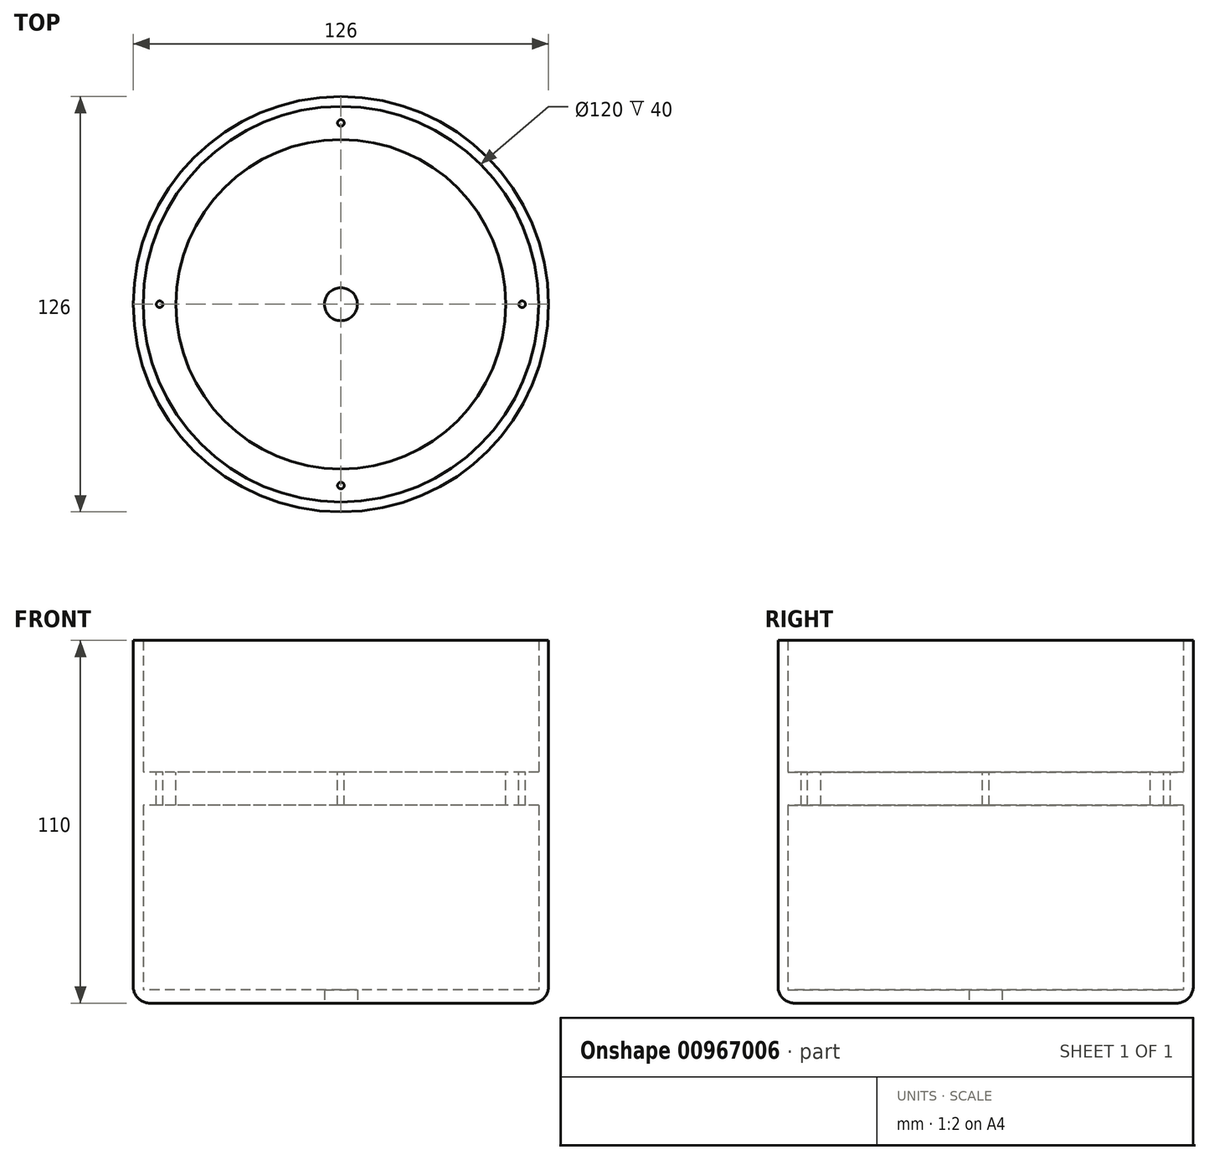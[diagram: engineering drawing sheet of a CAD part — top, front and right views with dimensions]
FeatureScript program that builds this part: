
annotation { "Feature Type Name" : "Feature", "Feature Type Description" : "" }
export const myFeature = defineFeature(function(context is Context, id is Id, definition is map)
    precondition{}
    {
        {
            var Q0;
            Q0=qCreatedBy(makeId("Top.planeOp"),FACE);
            var sketch = newSketch(context, id + "F0", { "sketchPlane" : qUnion([Q0])});
            skCircle(sketch, "E0", {"center": v(0, 0) * mm, "radius": 60 * mm});
            skCircle(sketch, "E1", {"center": v(0, 0) * mm, "radius": 63 * mm});
            skCircle(sketch, "E2", {"center": v(0, 0) * mm, "radius": 50 * mm});
            skCircle(sketch, "E3", {"center": v(0, 55) * mm, "radius": 1 * mm});
            skCircle(sketch, "E4", {"center": v(0, -55) * mm, "radius": 1 * mm});
            skCircle(sketch, "E5", {"center": v(55, 0) * mm, "radius": 1 * mm});
            skCircle(sketch, "E6", {"center": v(-55, 0) * mm, "radius": 1 * mm});
            skSolve(sketch);
        }
        {
            var Q0;
            Q0=makeQuery(id+"F0.imprint","IMPRINT",FACE,{"disambiguationData":[TD([[makeQuery(id+"F0.imprint","IMPRINT",EDGE,{"derivedFrom":sQuery(id+"F0.wireOp",EDGE,"E0")}),-1.0]])]});
            extrude(context, id + "F1", {"entities" : qUnion([Q0]), "depth" : 40 * mm, "offsetDistance" : 25 * mm});
        }
        {
            var Q0;
            Q0=makeQuery(id+"F0.imprint","IMPRINT",FACE,{"disambiguationData":[TD([[makeQuery(id+"F0.imprint","IMPRINT",EDGE,{"derivedFrom":sQuery(id+"F0.wireOp",EDGE,"E0")}),-1.0]])]});
            extrude(context, id + "F2", {"entities" : qUnion([Q0]), "operationType" : NewBodyOperationType.ADD, "oppositeDirection" : true, "depth" : 70 * mm, "offsetDistance" : 25 * mm});
        }
        {
            var Q0;
            Q0=makeQuery(id+"F0.imprint","IMPRINT",FACE,{"disambiguationData":[TD([[makeQuery(id+"F0.imprint","IMPRINT",EDGE,{"derivedFrom":sQuery(id+"F0.wireOp",EDGE,"E0")}),1.0]])]});
            extrude(context, id + "F3", {"entities" : qUnion([Q0]), "operationType" : NewBodyOperationType.ADD, "oppositeDirection" : true, "depth" : 10 * mm, "offsetDistance" : 25 * mm});
        }
        {
            var Q0;
            Q0=makeQuery(id+"F2.opExtrude","CAP_FACE",FACE,{"disambiguationData":[OSD([sQuery(id+"F0.wireOp",EDGE,"E0"),sQuery(id+"F0.wireOp",EDGE,"E1")])],"isStart":false});
            var sketch = newSketch(context, id + "F4", { "sketchPlane" : qUnion([Q0])});
            skCircle(sketch, "E7", {"center": v(0, 0) * mm, "radius": 60 * mm});
            skCircle(sketch, "E8", {"center": v(0, 0) * mm, "radius": 5 * mm});
            skSolve(sketch);
        }
        {
            var Q0;
            Q0=makeQuery(id+"F4.imprint","IMPRINT",FACE,{"disambiguationData":[TD([[makeQuery(id+"F4.imprint","IMPRINT",EDGE,{"derivedFrom":sQuery(id+"F4.wireOp",EDGE,"E7")}),-1.0]])]});
            extrude(context, id + "F5", {"entities" : qUnion([Q0]), "operationType" : NewBodyOperationType.ADD, "oppositeDirection" : true, "depth" : 4 * mm, "offsetDistance" : 25 * mm});
        }
        {
            var Q0;
            Q0=makeQuery(id+"F2.opExtrude","CAP_EDGE",EDGE,{"disambiguationData":[OSD([sQuery(id+"F0.wireOp",EDGE,"E1")])],"isStart":false});
            var Q1;
            Q1=makeQuery(id+"F5.opExtrude","CAP_EDGE",EDGE,{"disambiguationData":[OSD([sQuery(id+"F4.wireOp",EDGE,"E7")])],"isStart":false});
            fillet(context, id + "F6", {"entities" : qUnion([Q0, Q1]), "radius" : 5 * mm, "tangentPropagation" : true, "allowEdgeOverflow" : false});
        }
    });
